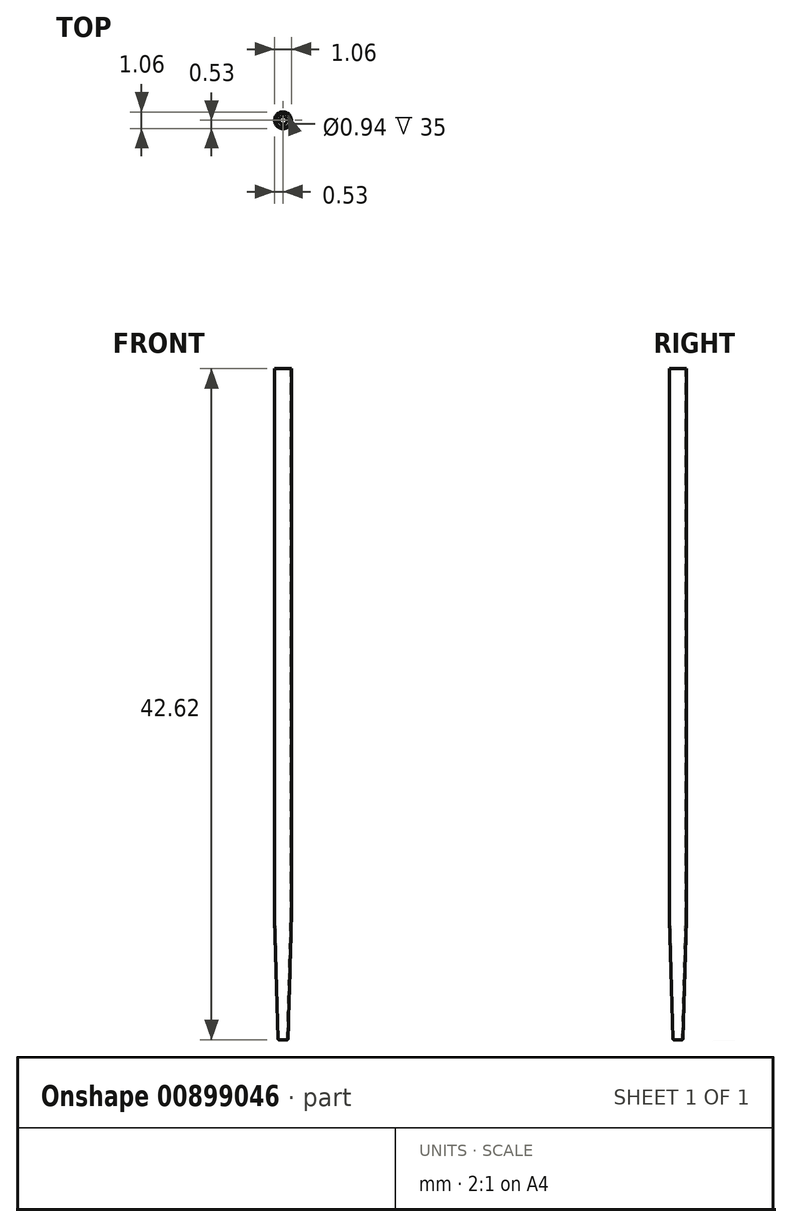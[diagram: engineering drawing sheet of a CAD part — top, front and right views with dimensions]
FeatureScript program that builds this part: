
annotation { "Feature Type Name" : "Feature", "Feature Type Description" : "" }
export const myFeature = defineFeature(function(context is Context, id is Id, definition is map)
    precondition{}
    {
        {
            var Q0;
            Q0=qCreatedBy(makeId("Front.planeOp"),FACE);
            var sketch = newSketch(context, id + "F0", { "sketchPlane" : qUnion([Q0])});
            skLineSegment(sketch, "E0", {"start": v(0, 3.2) * mm, "end": v(0, -2.26) * mm, "construction": true});
            skLineSegment(sketch, "E1", {"start": v(-0.25, 0) * mm, "end": v(-0.47, 7.62) * mm});
            skLineSegment(sketch, "E2", {"start": v(-0.47, 7.62) * mm, "end": v(-0.47, 42.62) * mm});
            skLineSegment(sketch, "E3", {"start": v(-0.32, 0.05) * mm, "end": v(-0.53, 7.62) * mm});
            skLineSegment(sketch, "E4", {"start": v(-0.53, 7.62) * mm, "end": v(-0.53, 42.62) * mm});
            skLineSegment(sketch, "E5", {"start": v(-0.53, 42.62) * mm, "end": v(-0.47, 42.62) * mm});
            skLineSegment(sketch, "E6", {"start": v(-0.26, 0) * mm, "end": v(-0.27, 0) * mm});
            skPoint(sketch, "E7.visualSharp", {"position": v(-0.32, 0) * mm});
            skArc(sketch, "E7.filletArc", {"start": v(-0.32, 0.05) * mm, "mid": v(-0.3, 0.01) * mm, "end": v(-0.27, 0) * mm});
            skPoint(sketch, "E8.visualSharp", {"position": v(-0.25, 0) * mm});
            skArc(sketch, "E8.filletArc", {"start": v(-0.26, 0) * mm, "mid": v(-0.26, 0) * mm, "end": v(-0.25, 0) * mm});
            skPoint(sketch, "E9.visualSharp", {"position": v(-0.53, 7.62) * mm});
            skArc(sketch, "E9.filletArc", {"start": v(-0.53, 7.62) * mm, "mid": v(-0.53, 7.62) * mm, "end": v(-0.53, 7.62) * mm});
            skPoint(sketch, "E10.visualSharp", {"position": v(-0.47, 7.62) * mm});
            skArc(sketch, "E10.filletArc", {"start": v(-0.47, 7.62) * mm, "mid": v(-0.47, 7.62) * mm, "end": v(-0.47, 7.62) * mm});
            skSolve(sketch);
        }
        {
            var Q0;
            Q0=makeQuery(id+"F0.imprint","IMPRINT",FACE,{"disambiguationData":[TD([[makeQuery(id+"F0.imprint","IMPRINT",EDGE,{"derivedFrom":sQuery(id+"F0.wireOp",EDGE,"E1")}),1.0]])]});
            var Q1;
            Q1=sQuery(id+"F0.wireOp",EDGE,"E0");
            revolve(context, id + "F1", {"surfaceOperationType" : NewSurfaceOperationType.NEW, "entities" : qUnion([Q0]), "axis" : qUnion([Q1]), "revolveType" : RevolveType.FULL});
        }
    });
